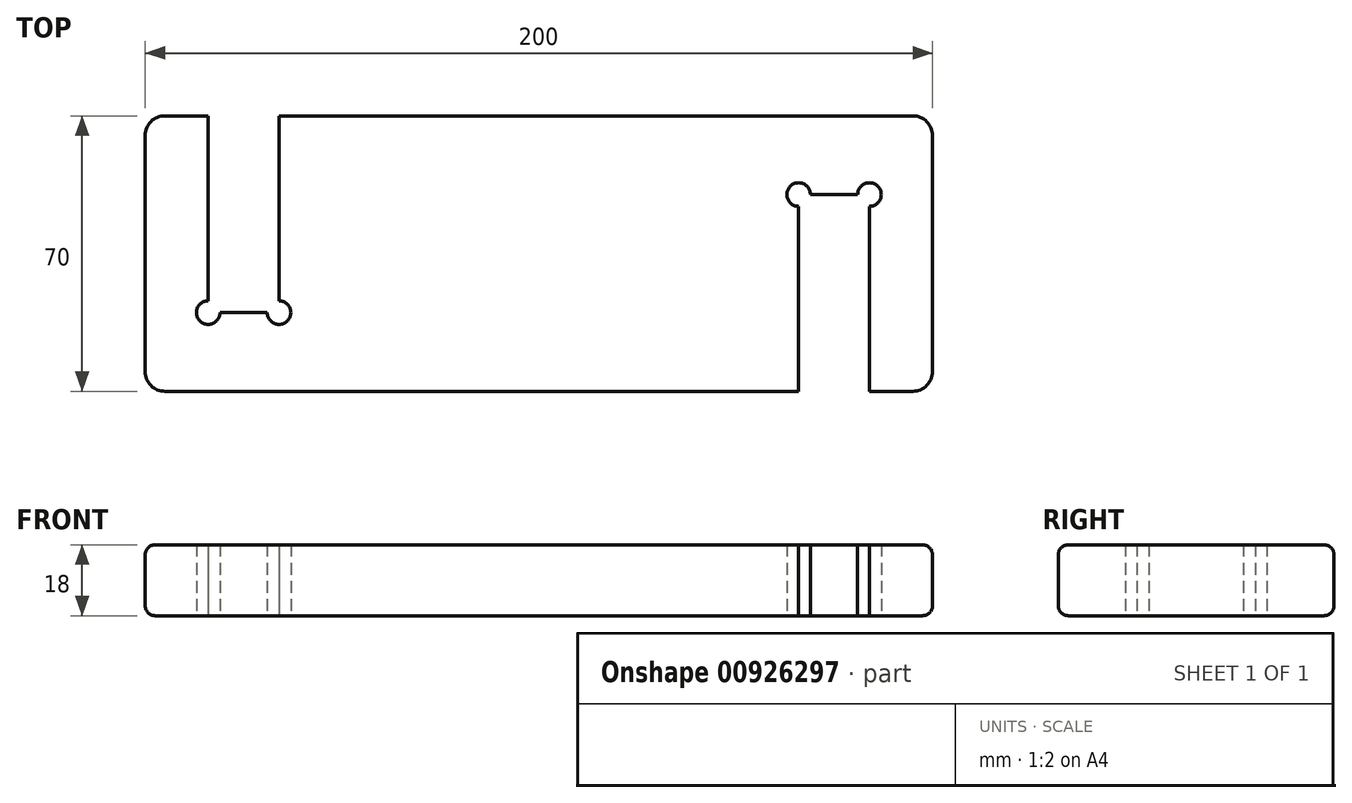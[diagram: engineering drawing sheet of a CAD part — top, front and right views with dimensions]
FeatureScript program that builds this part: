
annotation { "Feature Type Name" : "Feature", "Feature Type Description" : "" }
export const myFeature = defineFeature(function(context is Context, id is Id, definition is map)
    precondition{}
    {
        {
            var Q0;
            Q0=qCreatedBy(makeId("Top.planeOp"),FACE);
            var sketch = newSketch(context, id + "F0", { "sketchPlane" : qUnion([Q0])});
            skLineSegment(sketch, "E0", {"start": v(0, 0) * mm, "end": v(166, 0) * mm});
            skLineSegment(sketch, "E1", {"start": v(0, 70) * mm, "end": v(16, 70) * mm});
            skLineSegment(sketch, "E2", {"start": v(200, 70) * mm, "end": v(200, 0) * mm});
            skLineSegment(sketch, "E3", {"start": v(16, 20) * mm, "end": v(16, 70) * mm});
            skLineSegment(sketch, "E4", {"start": v(16, 20) * mm, "end": v(34, 20) * mm});
            skLineSegment(sketch, "E5", {"start": v(34, 20) * mm, "end": v(34, 70) * mm});
            skLineSegment(sketch, "E6.trimOffspring", {"start": v(34, 70) * mm, "end": v(200, 70) * mm});
            skLineSegment(sketch, "E7", {"start": v(0, 0) * mm, "end": v(0, 70) * mm});
            skLineSegment(sketch, "E8", {"start": v(166, 0) * mm, "end": v(166, 50) * mm});
            skLineSegment(sketch, "E9", {"start": v(166, 50) * mm, "end": v(184, 50) * mm});
            skLineSegment(sketch, "E10", {"start": v(184, 50) * mm, "end": v(184, 0) * mm});
            skLineSegment(sketch, "E11", {"start": v(184, 0) * mm, "end": v(200, 0) * mm});
            skCircle(sketch, "E12", {"center": v(166, 50) * mm, "radius": 3 * mm});
            skCircle(sketch, "E13", {"center": v(184, 50) * mm, "radius": 3 * mm});
            skCircle(sketch, "E14", {"center": v(34, 20) * mm, "radius": 3 * mm});
            skCircle(sketch, "E15", {"center": v(16, 20) * mm, "radius": 3 * mm});
            skSolve(sketch);
        }
        {
            var Q0;
            Q0=makeQuery(id+"F0.imprint","IMPRINT",FACE,{"disambiguationData":[TD([[makeQuery(id+"F0.imprint","IMPRINT",EDGE,{"derivedFrom":sQuery(id+"F0.wireOp",EDGE,"E0")}),1.0]])]});
            extrude(context, id + "F1", {"entities" : qUnion([Q0]), "depth" : 18 * mm, "offsetDistance" : 25 * mm});
        }
        {
            var Q0;
            Q0=makeQuery(id+"F1.opExtrude","SWEPT_EDGE",EDGE,{"disambiguationData":[OSD([sQuery(id+"F0.wireOp",EDGE,"E0"),sQuery(id+"F0.wireOp",EDGE,"E7")])]});
            var Q1;
            Q1=makeQuery(id+"F1.opExtrude","SWEPT_EDGE",EDGE,{"disambiguationData":[OSD([sQuery(id+"F0.wireOp",EDGE,"E2"),sQuery(id+"F0.wireOp",EDGE,"E6.trimOffspring")])]});
            var Q2;
            Q2=makeQuery(id+"F1.opExtrude","SWEPT_EDGE",EDGE,{"disambiguationData":[OSD([sQuery(id+"F0.wireOp",EDGE,"E2"),sQuery(id+"F0.wireOp",EDGE,"E11")])]});
            var Q3;
            Q3=makeQuery(id+"F1.opExtrude","SWEPT_EDGE",EDGE,{"disambiguationData":[OSD([sQuery(id+"F0.wireOp",EDGE,"E1"),sQuery(id+"F0.wireOp",EDGE,"E7")])]});
            fillet(context, id + "F2", {"entities" : qUnion([Q0, Q1, Q2, Q3]), "radius" : 5 * mm, "tangentPropagation" : true, "allowEdgeOverflow" : false});
        }
        {
            var Q0;
            Q0=makeQuery(id+"F1.opExtrude","CAP_EDGE",EDGE,{"disambiguationData":[OSD([sQuery(id+"F0.wireOp",EDGE,"E0")])],"isStart":false});
            var Q1;
            Q1=makeQuery(id+"F1.opExtrude","CAP_EDGE",EDGE,{"disambiguationData":[OSD([sQuery(id+"F0.wireOp",EDGE,"E0")])],"isStart":true});
            var Q2;
            Q2=makeQuery(id+"F1.opExtrude","CAP_EDGE",EDGE,{"disambiguationData":[OSD([sQuery(id+"F0.wireOp",EDGE,"E6.trimOffspring")])],"isStart":false});
            var Q3;
            Q3=makeQuery(id+"F1.opExtrude","CAP_EDGE",EDGE,{"disambiguationData":[OSD([sQuery(id+"F0.wireOp",EDGE,"E2")])],"isStart":true});
            fillet(context, id + "F3", {"entities" : qUnion([Q0, Q1, Q2, Q3]), "radius" : 2.5 * mm, "tangentPropagation" : true, "allowEdgeOverflow" : false});
        }
    });
